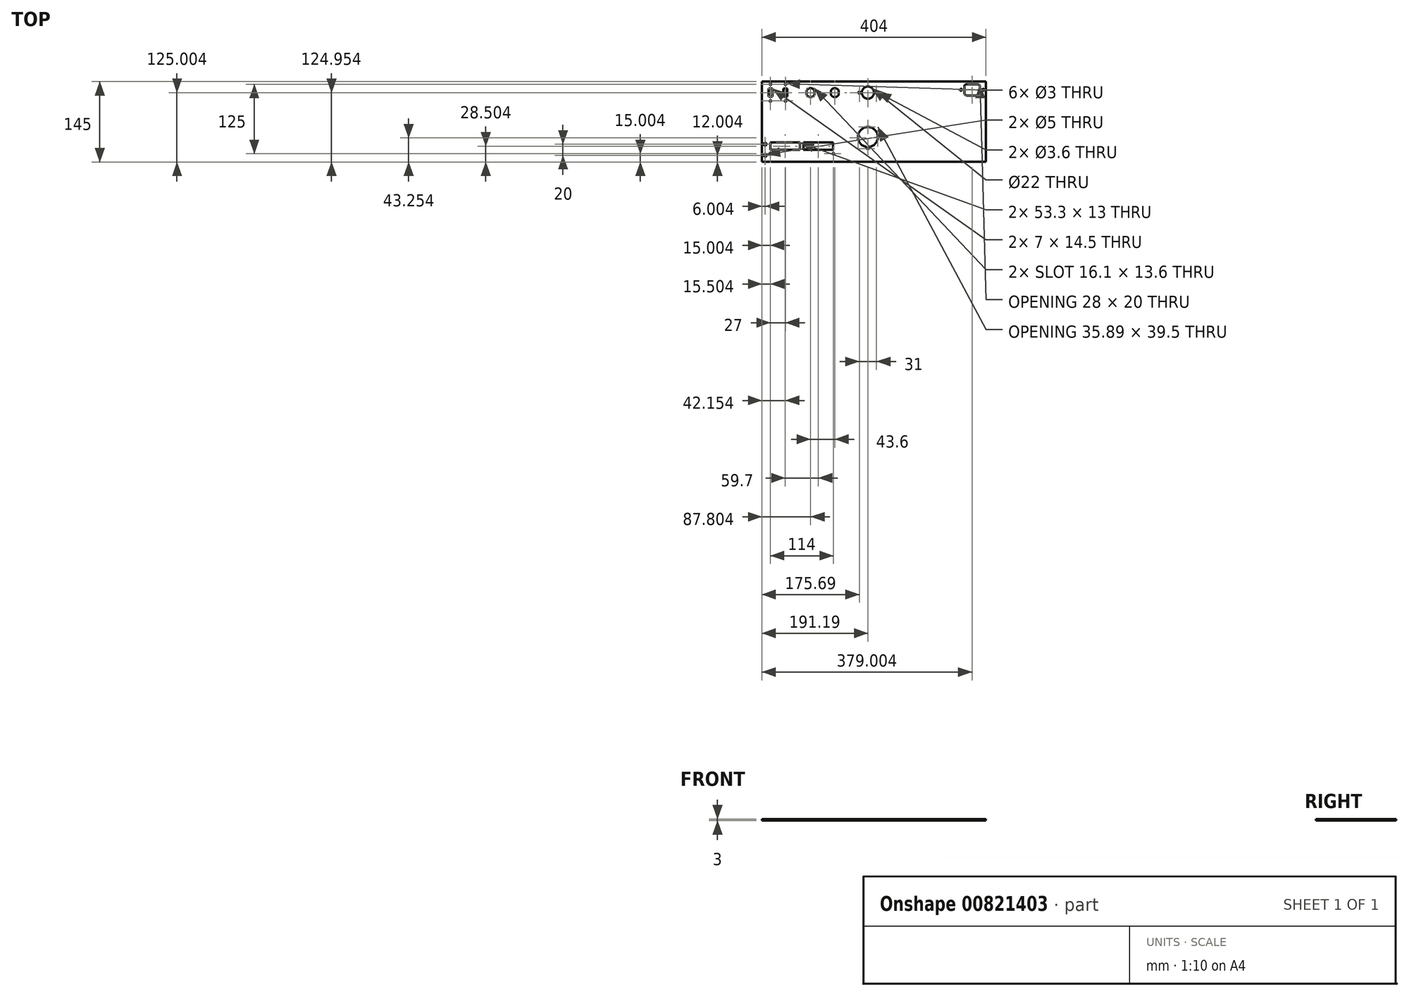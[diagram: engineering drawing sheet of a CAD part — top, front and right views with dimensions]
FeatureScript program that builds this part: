
annotation { "Feature Type Name" : "Feature", "Feature Type Description" : "" }
export const myFeature = defineFeature(function(context is Context, id is Id, definition is map)
    precondition{}
    {
        {
            var Q0;
            Q0=qCreatedBy(makeId("Top.planeOp"),FACE);
            var sketch = newSketch(context, id + "F0", { "sketchPlane" : qUnion([Q0])});
            skLineSegment(sketch, "E0.bottom", {"start": v(-216.19, 64.87) * mm, "end": v(187.81, 64.87) * mm});
            skLineSegment(sketch, "E0.top", {"start": v(-216.19, -80.13) * mm, "end": v(187.81, -80.13) * mm});
            skLineSegment(sketch, "E0.left", {"start": v(-216.19, 64.87) * mm, "end": v(-216.19, -80.13) * mm});
            skLineSegment(sketch, "E0.right", {"start": v(187.81, 64.87) * mm, "end": v(187.81, -80.13) * mm});
            skSolve(sketch);
        }
        {
            var Q0;
            Q0=qCreatedBy(makeId("Top.planeOp"),FACE);
            var sketch = newSketch(context, id + "F1", { "sketchPlane" : qUnion([Q0])});
            skCircle(sketch, "E1", {"center": v(-210.19, -68.13) * mm, "radius": 2.5 * mm});
            skArc(sketch, "E2", {"start": v(-135.19, 40.57) * mm, "mid": v(-128.39, 36.82) * mm, "end": v(-121.59, 40.57) * mm});
            skLineSegment(sketch, "E3", {"start": v(-135.19, 49.18) * mm, "end": v(-135.19, 40.57) * mm});
            skLineSegment(sketch, "E4", {"start": v(-121.59, 49.18) * mm, "end": v(-121.59, 40.57) * mm});
            skArc(sketch, "E5.trimOffspring", {"start": v(-121.59, 49.18) * mm, "mid": v(-128.39, 52.92) * mm, "end": v(-135.19, 49.18) * mm});
            skCircle(sketch, "E6", {"center": v(-25, -35.13) * mm, "radius": 18 * mm});
            skLineSegment(sketch, "E7.bottom", {"start": v(-27.75, -56.63) * mm, "end": v(-22.25, -56.63) * mm});
            skLineSegment(sketch, "E7.top", {"start": v(-27.75, -31.4) * mm, "end": v(-22.25, -31.4) * mm});
            skLineSegment(sketch, "E7.left", {"start": v(-27.75, -56.63) * mm, "end": v(-27.75, -31.4) * mm});
            skLineSegment(sketch, "E7.right", {"start": v(-22.25, -56.63) * mm, "end": v(-22.25, -31.4) * mm});
            skCircle(sketch, "E8", {"center": v(-25, 44.87) * mm, "radius": 11 * mm});
            skCircle(sketch, "E9", {"center": v(-40.5, 44.87) * mm, "radius": 1.8 * mm});
            skCircle(sketch, "E10.MirrorC", {"center": v(-9.5, 44.87) * mm, "radius": 1.8 * mm});
            skCircle(sketch, "E11.0.1.0", {"center": v(-210.19, -48.13) * mm, "radius": 2.5 * mm});
            skLineSegment(sketch, "E11.direction1", {"start": v(-210.19, -68.13) * mm, "end": v(-163.19, -68.13) * mm, "construction": true});
            skLineSegment(sketch, "E11.direction2", {"start": v(-210.19, -68.13) * mm, "end": v(-210.19, -48.13) * mm, "construction": true});
            skLineSegment(sketch, "E12.bottom", {"start": v(172.81, 39.87) * mm, "end": v(152.81, 39.87) * mm});
            skLineSegment(sketch, "E12.top", {"start": v(172.81, 59.87) * mm, "end": v(152.81, 59.87) * mm});
            skLineSegment(sketch, "E12.left", {"start": v(176.81, 43.87) * mm, "end": v(176.81, 55.87) * mm});
            skLineSegment(sketch, "E12.right", {"start": v(148.81, 43.87) * mm, "end": v(148.81, 55.87) * mm});
            skPoint(sketch, "E12.middle", {"position": v(162.81, 49.87) * mm});
            skCircle(sketch, "E13", {"center": v(142.81, 49.87) * mm, "radius": 1.75 * mm});
            skCircle(sketch, "E14", {"center": v(182.81, 49.87) * mm, "radius": 1.75 * mm});
            skPoint(sketch, "E15.visualSharp", {"position": v(148.81, 59.87) * mm});
            skArc(sketch, "E15.filletArc", {"start": v(152.81, 59.87) * mm, "mid": v(149.99, 58.7) * mm, "end": v(148.81, 55.87) * mm});
            skPoint(sketch, "E16.visualSharp", {"position": v(176.81, 59.87) * mm});
            skArc(sketch, "E16.filletArc", {"start": v(176.81, 55.87) * mm, "mid": v(175.64, 58.7) * mm, "end": v(172.81, 59.87) * mm});
            skPoint(sketch, "E17.visualSharp", {"position": v(176.81, 39.87) * mm});
            skArc(sketch, "E17.filletArc", {"start": v(172.81, 39.87) * mm, "mid": v(175.64, 41.05) * mm, "end": v(176.81, 43.87) * mm});
            skPoint(sketch, "E18.visualSharp", {"position": v(148.81, 39.87) * mm});
            skArc(sketch, "E18.filletArc", {"start": v(148.81, 43.87) * mm, "mid": v(149.99, 41.05) * mm, "end": v(152.81, 39.87) * mm});
            skLineSegment(sketch, "E19.bottom", {"start": v(-204.19, 11.87) * mm, "end": v(-84.19, 11.87) * mm, "construction": true});
            skLineSegment(sketch, "E19.top", {"start": v(-204.19, -68.13) * mm, "end": v(-84.19, -68.13) * mm, "construction": true});
            skLineSegment(sketch, "E19.left", {"start": v(-204.19, 11.87) * mm, "end": v(-204.19, -68.13) * mm, "construction": true});
            skLineSegment(sketch, "E19.right", {"start": v(-84.19, 11.87) * mm, "end": v(-84.19, -68.13) * mm, "construction": true});
            skLineSegment(sketch, "E20.bottom", {"start": v(-147.39, -45.13) * mm, "end": v(-200.69, -45.13) * mm});
            skLineSegment(sketch, "E20.top", {"start": v(-147.39, -58.13) * mm, "end": v(-200.69, -58.13) * mm});
            skLineSegment(sketch, "E20.left", {"start": v(-147.39, -45.13) * mm, "end": v(-147.39, -58.13) * mm});
            skLineSegment(sketch, "E20.right", {"start": v(-200.69, -45.13) * mm, "end": v(-200.69, -58.13) * mm});
            skPoint(sketch, "E20.middle", {"position": v(-174.04, -51.63) * mm});
            skLineSegment(sketch, "E21.bottom", {"start": v(-87.69, -45.13) * mm, "end": v(-140.99, -45.13) * mm});
            skLineSegment(sketch, "E21.top", {"start": v(-87.69, -58.13) * mm, "end": v(-140.99, -58.13) * mm});
            skLineSegment(sketch, "E21.left", {"start": v(-87.69, -45.13) * mm, "end": v(-87.69, -58.13) * mm});
            skLineSegment(sketch, "E21.right", {"start": v(-140.99, -45.13) * mm, "end": v(-140.99, -58.13) * mm});
            skPoint(sketch, "E21.middle", {"position": v(-114.34, -51.63) * mm});
            skLineSegment(sketch, "E22.bottom", {"start": v(-197.19, 37.57) * mm, "end": v(-204.19, 37.57) * mm});
            skLineSegment(sketch, "E22.top", {"start": v(-197.19, 52.07) * mm, "end": v(-204.19, 52.07) * mm});
            skLineSegment(sketch, "E22.left", {"start": v(-197.19, 37.57) * mm, "end": v(-197.19, 52.07) * mm});
            skLineSegment(sketch, "E22.right", {"start": v(-204.19, 37.57) * mm, "end": v(-204.19, 52.07) * mm});
            skPoint(sketch, "E22.middle", {"position": v(-200.69, 44.82) * mm});
            skCircle(sketch, "E23", {"center": v(-200.69, 59.87) * mm, "radius": 1.5 * mm});
            skCircle(sketch, "E24", {"center": v(-200.69, 29.77) * mm, "radius": 1.5 * mm});
            skLineSegment(sketch, "E25.bottom", {"start": v(-170.19, 37.57) * mm, "end": v(-177.19, 37.57) * mm});
            skLineSegment(sketch, "E25.top", {"start": v(-170.19, 52.07) * mm, "end": v(-177.19, 52.07) * mm});
            skLineSegment(sketch, "E25.left", {"start": v(-170.19, 37.57) * mm, "end": v(-170.19, 52.07) * mm});
            skLineSegment(sketch, "E25.right", {"start": v(-177.19, 37.57) * mm, "end": v(-177.19, 52.07) * mm});
            skPoint(sketch, "E25.middle", {"position": v(-173.69, 44.82) * mm});
            skCircle(sketch, "E26", {"center": v(-173.69, 59.87) * mm, "radius": 1.5 * mm});
            skCircle(sketch, "E27", {"center": v(-173.69, 29.77) * mm, "radius": 1.5 * mm});
            skArc(sketch, "E28", {"start": v(-91.59, 40.57) * mm, "mid": v(-84.79, 36.82) * mm, "end": v(-77.99, 40.57) * mm});
            skLineSegment(sketch, "E29", {"start": v(-91.59, 49.18) * mm, "end": v(-91.59, 40.57) * mm});
            skLineSegment(sketch, "E30", {"start": v(-77.99, 49.18) * mm, "end": v(-77.99, 40.57) * mm});
            skArc(sketch, "E31.trimOffspring", {"start": v(-77.99, 49.18) * mm, "mid": v(-84.79, 52.92) * mm, "end": v(-91.59, 49.18) * mm});
            skLineSegment(sketch, "E32.bottom", {"start": v(12.81, 29.87) * mm, "end": v(182.81, 29.87) * mm, "construction": true});
            skLineSegment(sketch, "E32.top", {"start": v(12.81, -80.13) * mm, "end": v(182.81, -80.13) * mm, "construction": true});
            skLineSegment(sketch, "E32.left", {"start": v(12.81, 29.87) * mm, "end": v(12.81, -80.13) * mm, "construction": true});
            skLineSegment(sketch, "E32.right", {"start": v(182.81, 29.87) * mm, "end": v(182.81, -80.13) * mm, "construction": true});
            skCircle(sketch, "E33", {"center": v(-201.19, -65.13) * mm, "radius": 1.5 * mm});
            skCircle(sketch, "E34", {"center": v(-87.19, -65.13) * mm, "radius": 1.5 * mm});
            skSolve(sketch);
        }
        {
            var Q0;
            Q0=makeQuery(id+"F0.imprint","IMPRINT",FACE,{"disambiguationData":[TD([[makeQuery(id+"F0.imprint","IMPRINT",EDGE,{"derivedFrom":sQuery(id+"F0.wireOp",EDGE,"E0.bottom")}),-1.0]])]});
            extrude(context, id + "F2", {"entities" : qUnion([Q0]), "oppositeDirection" : true, "depth" : 3 * mm, "offsetDistance" : 25 * mm});
        }
        {
            var Q0;
            Q0=qSketchRegion(id+"F1",true);
            extrude(context, id + "F3", {"entities" : qUnion([Q0]), "operationType" : NewBodyOperationType.REMOVE, "oppositeDirection" : true, "depth" : 25 * mm, "offsetDistance" : 25 * mm});
        }
    });
